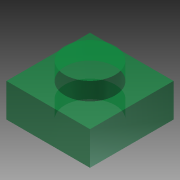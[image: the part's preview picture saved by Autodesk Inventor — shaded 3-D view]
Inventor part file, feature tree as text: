
AUTODESK INVENTOR PART (.ipt)
format: ipt  version: 2013 (Build 170138000, 138)  size: 107,520 bytes
history: native  units: mm
features: extrude x3, sketch x1, pattern_linear x1
ambient origin geometry x8: Origin, YZ Plane, XZ Plane, XY Plane, X Axis, Y Axis, Z Axis, Center Point
bodies: Solid1 (feature_tree)
feature tree (5):
  sketch  "Sketch1"  dims[d0=8.0mm d1=8.0mm d2=4.8mm d3=3.2mm d4=0.0mm d5=4.9mm d6=0.0mm d7=1.7mm d8=0.0mm d9=10.0mm d11=8.0mm d22=10.0mm d24=8.0mm]
  extrude  "Extrusion1"  Depth=8.0mm
  extrude  "Extrusion2"  Depth=4.8mm
  extrude  "Extrusion3"  Depth=3.2mm TaperAngle=0.0deg
  pattern_linear  "Rectangular Pattern1"  Spacing1=4.9mm  [1 undecoded]
note: 1 required parameter value undecoded (feature->parameter linkage not recoverable at this tier; creation-order binding heuristic only, values carry confidence <= 0.55)
